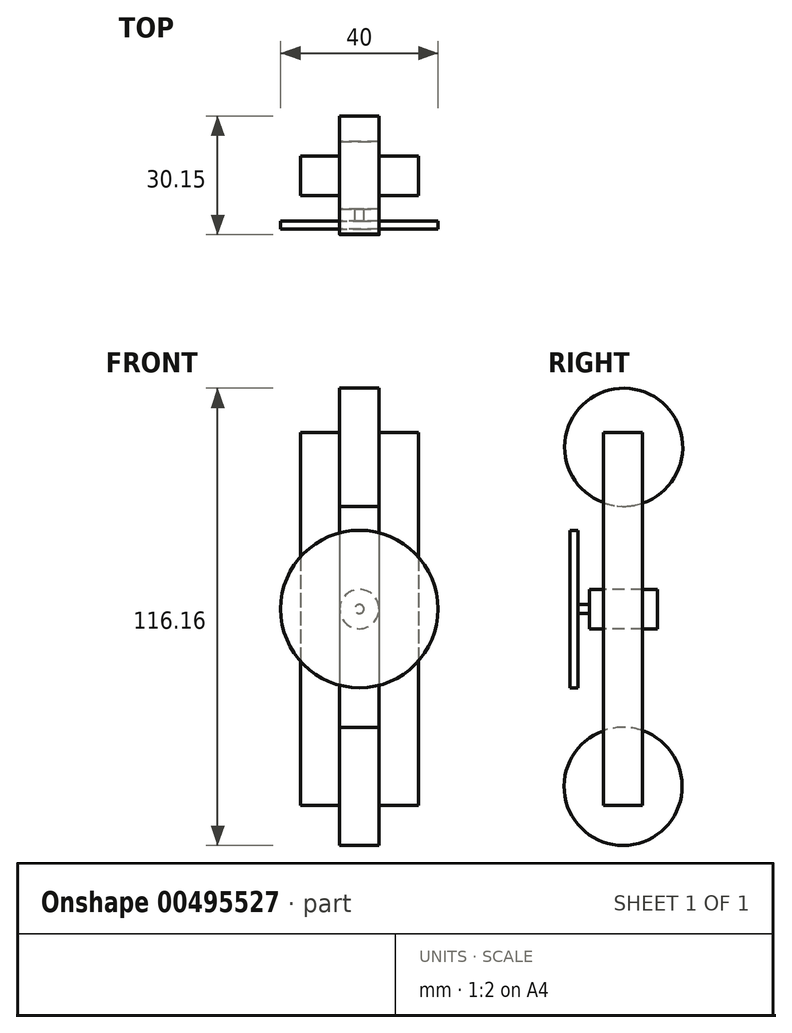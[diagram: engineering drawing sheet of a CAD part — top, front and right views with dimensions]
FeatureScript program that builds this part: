
annotation { "Feature Type Name" : "Feature", "Feature Type Description" : "" }
export const myFeature = defineFeature(function(context is Context, id is Id, definition is map)
    precondition{}
    {
        {
            var Q0;
            Q0=qCreatedBy(makeId("Front.planeOp"),FACE);
            var sketch = newSketch(context, id + "F0", { "sketchPlane" : qUnion([Q0])});
            skLineSegment(sketch, "E0.bottom", {"start": v(-15, 44.84) * mm, "end": v(-5, 44.84) * mm});
            skLineSegment(sketch, "E0.top", {"start": v(-15, -49.94) * mm, "end": v(-5, -49.94) * mm});
            skLineSegment(sketch, "E0.left", {"start": v(-15, 44.84) * mm, "end": v(-15, -49.94) * mm});
            skLineSegment(sketch, "E0.right", {"start": v(-5, 44.84) * mm, "end": v(-5, -49.94) * mm});
            skLineSegment(sketch, "E1", {"start": v(0, 60.53) * mm, "end": v(0, -57.78) * mm, "construction": true});
            skLineSegment(sketch, "E2.MirrorCS", {"start": v(5, 44.84) * mm, "end": v(5, -49.94) * mm});
            skLineSegment(sketch, "E3.MirrorCS", {"start": v(15, 44.84) * mm, "end": v(15, -49.94) * mm});
            skLineSegment(sketch, "E4.MirrorCS", {"start": v(15, -49.94) * mm, "end": v(5, -49.94) * mm});
            skLineSegment(sketch, "E5.MirrorCS", {"start": v(15, 44.84) * mm, "end": v(5, 44.84) * mm});
            skSolve(sketch);
        }
        {
            var Q0;
            Q0=makeQuery(id+"F0.imprint","IMPRINT",FACE,{"disambiguationData":[TD([[makeQuery(id+"F0.imprint","IMPRINT",EDGE,{"derivedFrom":sQuery(id+"F0.wireOp",EDGE,"E2.MirrorCS")}),1.0]])]});
            var Q1;
            Q1=makeQuery(id+"F0.imprint","IMPRINT",FACE,{"disambiguationData":[TD([[makeQuery(id+"F0.imprint","IMPRINT",EDGE,{"derivedFrom":sQuery(id+"F0.wireOp",EDGE,"E0.bottom")}),-1.0]])]});
            extrude(context, id + "F1", {"entities" : qUnion([Q0, Q1]), "depth" : 10 * mm});
        }
        {
            var Q0;
            Q0=makeQuery(id+"F1.opExtrude","SWEPT_FACE",FACE,{"disambiguationData":[OSD([sQuery(id+"F0.wireOp",EDGE,"E0.right")])]});
            var sketch = newSketch(context, id + "F2", { "sketchPlane" : qUnion([Q0])});
            skCircle(sketch, "E6", {"center": v(-4.94, -45.06) * mm, "radius": 15 * mm});
            skCircle(sketch, "E7", {"center": v(-4.8, 41.1) * mm, "radius": 15 * mm});
            skSolve(sketch);
        }
        {
            var Q0;
            Q0 = qSketchRegion(id + "F2", true);
            extrude(context, id + "F3", {"entities" : qUnion([Q0]), "depth" : 10 * mm});
        }
        {
            var Q0;
            Q0=makeQuery(id+"F1.opExtrude","CAP_FACE",FACE,{"disambiguationData":[OSD([sQuery(id+"F0.wireOp",EDGE,"E0.bottom"),sQuery(id+"F0.wireOp",EDGE,"E0.top"),sQuery(id+"F0.wireOp",EDGE,"E0.left"),sQuery(id+"F0.wireOp",EDGE,"E0.right")])],"isStart":false});
            var sketch = newSketch(context, id + "F4", { "sketchPlane" : qUnion([Q0])});
            skCircle(sketch, "E8", {"center": v(0, 0) * mm, "radius": 5 * mm});
            skSolve(sketch);
        }
        {
            var Q0;
            Q0 = qSketchRegion(id + "F4", true);
            extrude(context, id + "F5", {"entities" : qUnion([Q0]), "oppositeDirection" : true, "depth" : 13.77 * mm});
        }
        {
            var Q0;
            Q0=makeQuery(id+"F5.opExtrude","CAP_FACE",FACE,{"disambiguationData":[OSD([sQuery(id+"F4.wireOp",EDGE,"E8")])],"isStart":true});
            extrude(context, id + "F6", {"entities" : qUnion([Q0]), "operationType" : NewBodyOperationType.ADD, "depth" : 3.44 * mm});
        }
        {
            var Q0;
            Q0=makeQuery(id+"F6.opExtrude","CAP_FACE",FACE,{"disambiguationData":[OSD([sQuery(id+"F4.wireOp",EDGE,"E8")])],"isStart":false});
            var sketch = newSketch(context, id + "F7", { "sketchPlane" : qUnion([Q0])});
            skCircle(sketch, "E9", {"center": v(0, 0) * mm, "radius": 1.15 * mm});
            skSolve(sketch);
        }
        {
            var Q0;
            Q0=makeQuery(id+"F7.imprint","IMPRINT",FACE,{"disambiguationData":[TD([[makeQuery(id+"F7.imprint","IMPRINT",EDGE,{"derivedFrom":sQuery(id+"F7.wireOp",EDGE,"E9")}),1.0]])]});
            extrude(context, id + "F8", {"entities" : qUnion([Q0]), "operationType" : NewBodyOperationType.ADD, "depth" : 5 * mm});
        }
        {
            var Q0;
            Q0=makeQuery(id+"F8.opExtrude","CAP_FACE",FACE,{"disambiguationData":[OSD([sQuery(id+"F7.wireOp",EDGE,"E9")])],"isStart":false});
            var sketch = newSketch(context, id + "F9", { "sketchPlane" : qUnion([Q0])});
            skCircle(sketch, "E10", {"center": v(0, 0) * mm, "radius": 20 * mm});
            skSolve(sketch);
        }
        {
            var Q0;
            Q0 = qSketchRegion(id + "F9", true);
            extrude(context, id + "F10", {"entities" : qUnion([Q0]), "operationType" : NewBodyOperationType.ADD, "oppositeDirection" : true, "depth" : 2 * mm});
        }
    });
